# Revit family: Sanitary_Taps-Mixers_hansgrohe_32526USA-Metropol-Single-lever-basin-mix_25
name_source: partatom
category: Plumbing Fixtures
revit_build: Autodesk Revit 2018 (Build: 20170223_1515(x64)
units: mm (PartAtom-declared; Revit-internal decimal feet)

## family parameters
Always vertical = No
Cut with Voids When Loaded = No
OmniClass Number = 23.31.11.00
OmniClass Title = Faucets
Part Type = Normal
Room Calculation Point = No
Round Connector Dimension = Use Diameter
Shared = No
Work Plane-Based = Yes

## types (2) — shared parameters
Always visible = Yes
BIMobject category = Taps & Mixers
Default Elevation = 4' - 0"
Description = Metropol Single lever basin mixer for concealed installation wall-mounted with lever handle and spout 22.5 cm
Edition number = 1
IFC Classification = Valve
Manufacturer = Hansgrohe
Manufacturer name = hansgrohe
Model = 32526USA
OmniClass Code = 23-31 11 00
OmniClass Description = Faucets
Product Guid = f56ed517-1129-440e-a564-2bf9b8e2e2e0
Product SKU = 32526USA
Product data url = https://bimobject.com
Product family = Metropol
Product group = Basin mixers
Product name = 32526USA Metropol Single lever basin mixer for concealed installation wall-mounted with lever handle and spout 22.5 cm
Product url = https://www.hansgrohe.com
QR code = https://bimobject.com
URL = https://www.hansgrohe.com
Weight Net (Kg) = 2,4

## per-type parameters (varying)
| type | Material 1 |
| 001 Chrome | Hansgrohe - Metal - 001 Chrome |
| 821 Brushed Nickel | Hansgrohe - Metal - 821 Brushed Nickel |

## geometry (parser evidence)
native form markers: Sweep x2
no freeform markers — native parametric forms only
